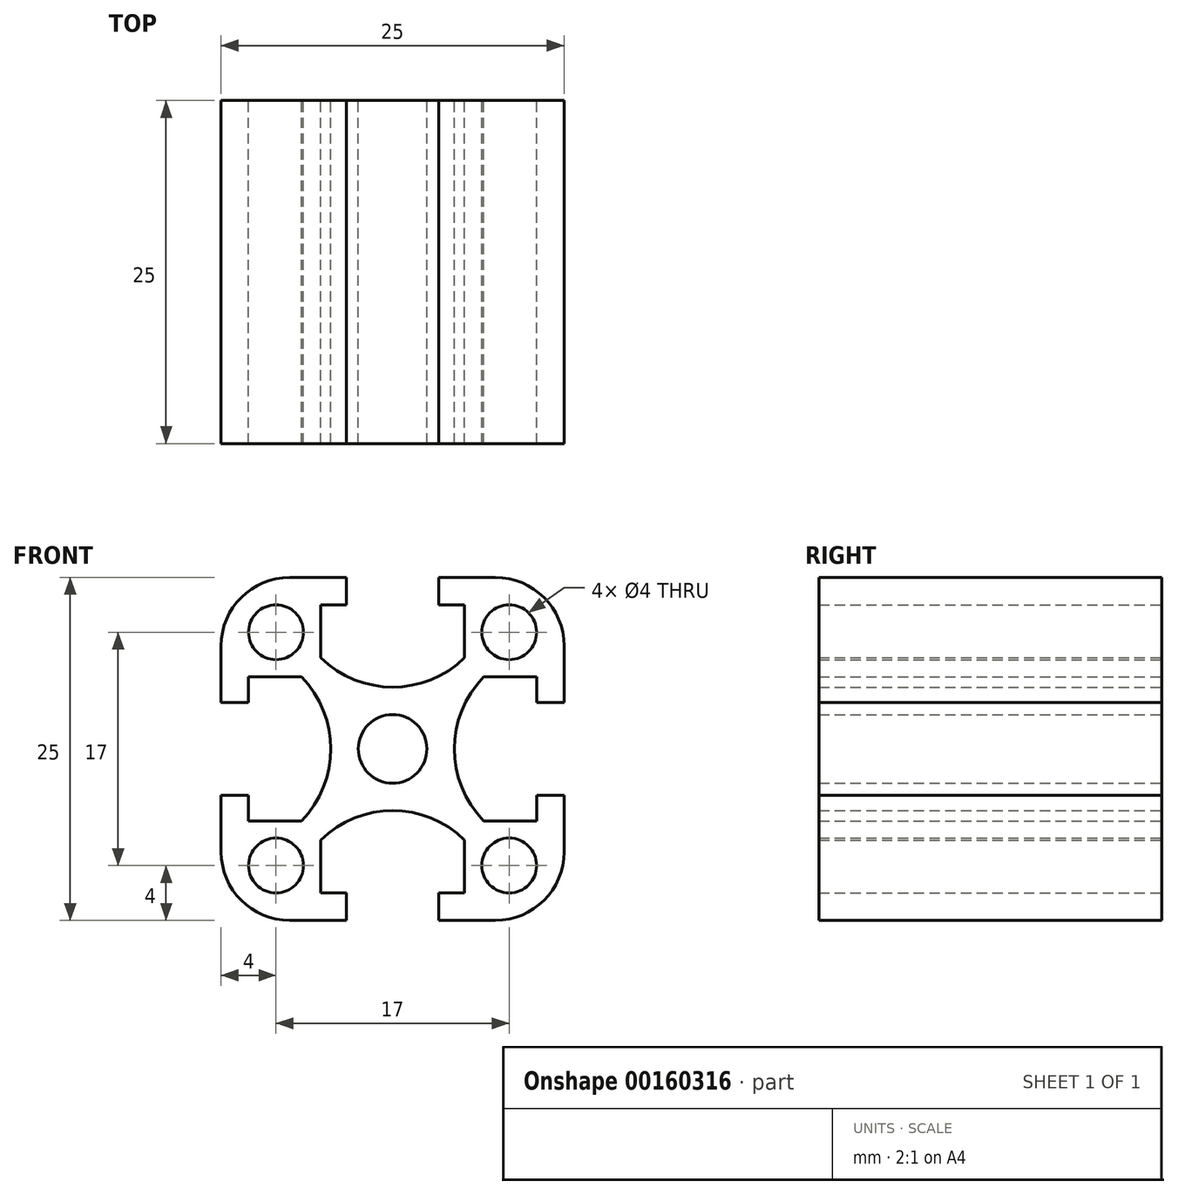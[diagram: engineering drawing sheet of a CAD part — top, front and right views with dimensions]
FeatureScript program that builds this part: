
annotation { "Feature Type Name" : "Feature", "Feature Type Description" : "" }
export const myFeature = defineFeature(function(context is Context, id is Id, definition is map)
    precondition{}
    {
        {
            var Q0;
            Q0=qCreatedBy(makeId("Front.planeOp"),FACE);
            var sketch = newSketch(context, id + "F0", { "sketchPlane" : qUnion([Q0])});
            skCircle(sketch, "E0", {"center": v(8.5, 8.5) * mm, "radius": 2 * mm});
            skCircle(sketch, "E1", {"center": v(-8.5, 8.5) * mm, "radius": 2 * mm});
            skCircle(sketch, "E2", {"center": v(-8.5, -8.5) * mm, "radius": 2 * mm});
            skCircle(sketch, "E3", {"center": v(0, 0) * mm, "radius": 2.5 * mm});
            skCircle(sketch, "E4", {"center": v(8.5, -8.5) * mm, "radius": 2 * mm});
            skLineSegment(sketch, "E5", {"start": v(-5.25, 6.64) * mm, "end": v(-5.25, 10.5) * mm});
            skLineSegment(sketch, "E6", {"start": v(-5.25, 10.5) * mm, "end": v(-3.38, 10.5) * mm});
            skLineSegment(sketch, "E7", {"start": v(-3.38, 10.5) * mm, "end": v(-3.38, 12.5) * mm});
            skLineSegment(sketch, "E8", {"start": v(-3.38, 12.5) * mm, "end": v(-7.5, 12.5) * mm});
            skArc(sketch, "E9", {"start": v(-7.5, 12.5) * mm, "mid": v(-11.04, 11.04) * mm, "end": v(-12.5, 7.5) * mm});
            skLineSegment(sketch, "E10", {"start": v(-12.5, 7.5) * mm, "end": v(-12.5, 3.37) * mm});
            skLineSegment(sketch, "E11", {"start": v(-12.5, 3.38) * mm, "end": v(-10.5, 3.38) * mm});
            skLineSegment(sketch, "E12", {"start": v(-10.5, 3.38) * mm, "end": v(-10.5, 5.25) * mm});
            skLineSegment(sketch, "E13", {"start": v(-10.5, 5.25) * mm, "end": v(-6.64, 5.25) * mm});
            skArc(sketch, "E14", {"start": v(-6.64, -5.25) * mm, "mid": v(-4.5, 0) * mm, "end": v(-6.64, 5.25) * mm});
            skLineSegment(sketch, "E15", {"start": v(-6.64, -5.25) * mm, "end": v(-10.5, -5.25) * mm});
            skLineSegment(sketch, "E16", {"start": v(-10.5, -5.25) * mm, "end": v(-10.5, -3.38) * mm});
            skLineSegment(sketch, "E17", {"start": v(-10.5, -3.38) * mm, "end": v(-12.5, -3.38) * mm});
            skLineSegment(sketch, "E18", {"start": v(-12.5, -3.38) * mm, "end": v(-12.5, -7.5) * mm});
            skArc(sketch, "E19", {"start": v(-12.5, -7.5) * mm, "mid": v(-11.04, -11.04) * mm, "end": v(-7.5, -12.5) * mm});
            skLineSegment(sketch, "E20", {"start": v(-7.5, -12.5) * mm, "end": v(-3.37, -12.5) * mm});
            skLineSegment(sketch, "E21", {"start": v(-3.38, -12.5) * mm, "end": v(-3.38, -10.5) * mm});
            skLineSegment(sketch, "E22", {"start": v(-3.38, -10.5) * mm, "end": v(-5.25, -10.5) * mm});
            skLineSegment(sketch, "E23", {"start": v(-5.25, -10.5) * mm, "end": v(-5.25, -6.64) * mm});
            skArc(sketch, "E24", {"start": v(5.25, -6.64) * mm, "mid": v(0, -4.5) * mm, "end": v(-5.25, -6.64) * mm});
            skLineSegment(sketch, "E25", {"start": v(5.25, -6.64) * mm, "end": v(5.25, -10.5) * mm});
            skLineSegment(sketch, "E26", {"start": v(5.25, -10.5) * mm, "end": v(3.38, -10.5) * mm});
            skLineSegment(sketch, "E27", {"start": v(3.38, -10.5) * mm, "end": v(3.38, -12.5) * mm});
            skLineSegment(sketch, "E28", {"start": v(3.38, -12.5) * mm, "end": v(7.5, -12.5) * mm});
            skArc(sketch, "E29", {"start": v(7.5, -12.5) * mm, "mid": v(11.04, -11.04) * mm, "end": v(12.5, -7.5) * mm});
            skLineSegment(sketch, "E30", {"start": v(12.5, -7.5) * mm, "end": v(12.5, -3.37) * mm});
            skLineSegment(sketch, "E31", {"start": v(12.5, -3.38) * mm, "end": v(10.5, -3.38) * mm});
            skLineSegment(sketch, "E32", {"start": v(10.5, -3.38) * mm, "end": v(10.5, -5.25) * mm});
            skLineSegment(sketch, "E33", {"start": v(10.5, -5.25) * mm, "end": v(6.64, -5.25) * mm});
            skArc(sketch, "E34", {"start": v(6.64, 5.25) * mm, "mid": v(4.5, 0) * mm, "end": v(6.64, -5.25) * mm});
            skLineSegment(sketch, "E35", {"start": v(6.64, 5.25) * mm, "end": v(10.5, 5.25) * mm});
            skLineSegment(sketch, "E36", {"start": v(10.5, 5.25) * mm, "end": v(10.5, 3.38) * mm});
            skLineSegment(sketch, "E37", {"start": v(10.5, 3.38) * mm, "end": v(12.5, 3.38) * mm});
            skLineSegment(sketch, "E38", {"start": v(12.5, 3.38) * mm, "end": v(12.5, 7.5) * mm});
            skArc(sketch, "E39", {"start": v(12.5, 7.5) * mm, "mid": v(11.04, 11.04) * mm, "end": v(7.5, 12.5) * mm});
            skLineSegment(sketch, "E40", {"start": v(7.5, 12.5) * mm, "end": v(3.37, 12.5) * mm});
            skLineSegment(sketch, "E41", {"start": v(3.38, 12.5) * mm, "end": v(3.38, 10.5) * mm});
            skLineSegment(sketch, "E42", {"start": v(3.38, 10.5) * mm, "end": v(5.25, 10.5) * mm});
            skLineSegment(sketch, "E43", {"start": v(5.25, 10.5) * mm, "end": v(5.25, 6.64) * mm});
            skArc(sketch, "E44", {"start": v(-5.25, 6.64) * mm, "mid": v(0, 4.5) * mm, "end": v(5.25, 6.64) * mm});
            skSolve(sketch);
        }
        {
            assignVariable(context, id + "F1", {"name" : "Length", "anyValue" : 25});
        }
        {
            var Q0;
            Q0 = qSketchRegion(id + "F0", true);
            extrude(context, id + "F2", {"entities" : qUnion([Q0]), "depth" : (getVariable(context, 'Length')) * mm});
        }
    });
